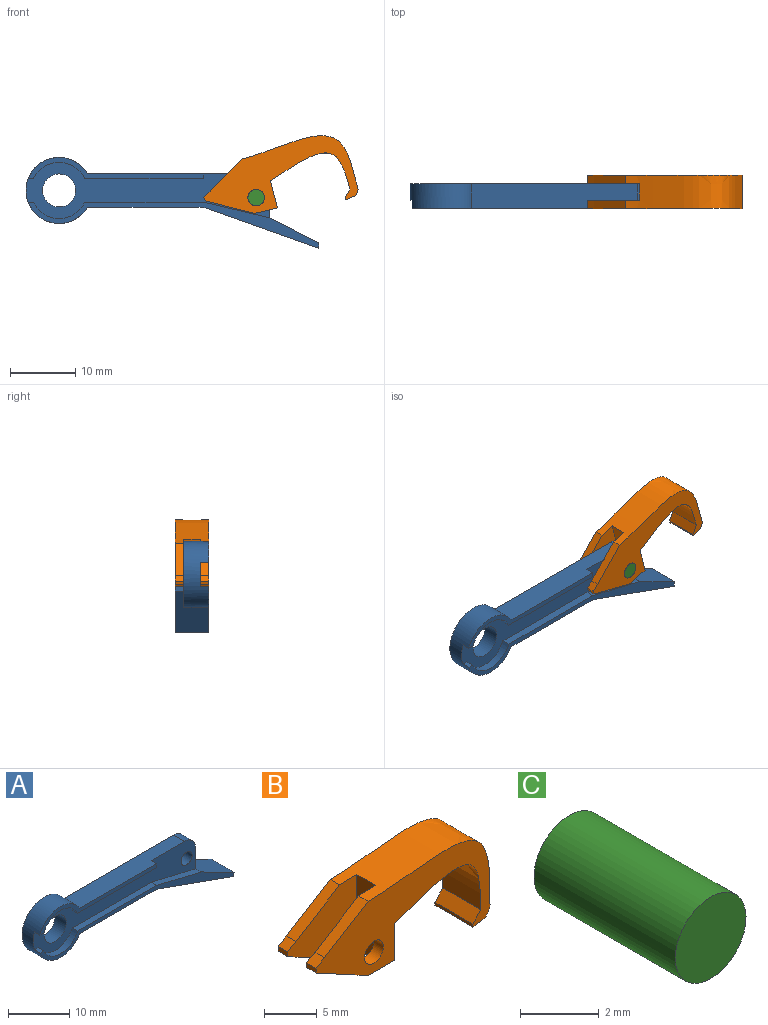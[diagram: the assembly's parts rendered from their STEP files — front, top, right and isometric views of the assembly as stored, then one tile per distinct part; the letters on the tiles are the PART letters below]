
ASSEMBLY  parts=3 mates=2
PART A: 26 faces, bbox 45x5.1x14 mm
  f0: plane 4.21x2.54mm, normal (1,0,0), area 10.7mm2, adj f1,f6,f7,f22
  f1: cylinder r=2.54mm len=2.54mm, axis (0,1,0), area 10.1mm2, adj f0,f2,f6,f7
  f2: plane 25.45x3.81mm, normal (0,0,1), area 87.2mm2, adj f1,f5,f6,f7,f11,f12
  f3: cylinder r=2.54mm len=5.08mm, axis (0,1,0), area 40.5mm2, adj f6,f7
  f4: cylinder r=1.27mm len=2.54mm, axis (0,1,0), area 20.3mm2, adj f6,f7
  f5: cylinder r=5.08mm len=10.16mm, axis (0,1,0), area 96.7mm2, adj f2,f6,f7,f8,f12,f13,f15,f17
  f6: plane 37.48x8.64mm, normal (0,-1,0), area 155.1mm2, adj f0,f1,f2,f3,f4,f5,f8,f9
  f7: plane 37.48x10.16mm, normal (0,1,0), area 198.9mm2, adj f0,f1,f2,f3,f4,f5,f15,f18
  f8: plane 1.27x0.82mm, normal (0,0,-1), area 1mm2, adj f5,f6,f9,f12
  f9: cylinder r=4.32mm len=7.88mm, axis (0,1,0), area 12.6mm2, adj f6,f8,f10,f12
  f10: plane 18.25x1.27mm, normal (0,0,-1), area 23.2mm2, adj f6,f9,f11,f12
  f11: plane 1.27x0.76mm, normal (1,0,0), area 1mm2, adj f2,f6,f10,f12
  f12: plane 26.94x3.31mm, normal (0,-1,0), area 21.9mm2, adj f2,f5,f8,f9,f10,f11
  f13: plane 1.27x0.82mm, normal (0,0,1), area 1mm2, adj f5,f6,f14,f17
  f14: cylinder r=4.32mm len=7.86mm, axis (0,1,0), area 12.6mm2, adj f6,f13,f16,f17
  f15: plane 16.9x3.81mm, normal (0,0,-1), area 64.4mm2, adj f5,f7,f17,f25
  f16: plane 18.26x1.27mm, normal (0,0,1), area 23.2mm2, adj f6,f14,f17,f23
  f17: plane 44.72x7.1mm, normal (0,-1,0), area 46.7mm2, adj f5,f13,f14,f15,f16,f20,f21,f22
  f18: plane 1.27x0.76mm, normal (-1,0,0.02), area 1mm2, adj f7,f19,f20,f24
  f19: plane 10.2x2.43mm, normal (0.23,0,0.97), area 13.3mm2, adj f7,f18,f22,f24
  f20: plane 17.78x6.34mm, normal (-0.34,0,-0.94), area 92.5mm2, adj f7,f17,f18,f21,f24,f25
  f21: plane 5.08x0.87mm, normal (1,0,-0.01), area 4.4mm2, adj f17,f20,f22,f24
  f22: plane 7.57x5.08mm, normal (0.45,0,0.89), area 43mm2, adj f0,f17,f19,f21,f23,f24
  f23: plane 10.2x2.43mm, normal (0.23,0,0.97), area 13.3mm2, adj f6,f16,f17,f22
  f24: plane 17.79x7.1mm, normal (0,1,0), area 24.8mm2, adj f18,f19,f20,f21,f22
  f25: cylinder r=5.08mm len=3.81mm, axis (0,1,0), area 6.6mm2, adj f7,f15,f17,f20
PART B: 23 faces, bbox 24x5.2x11.4 mm
  f0: plane 5.08x4.3mm, normal (1,0,0), area 21.9mm2, adj f1,f13,f14,f18
  f1: plane 5.08x3.55mm, normal (0,0,-1), area 12.2mm2, adj f0,f2,f11,f13,f14,f15,f16,f17
  f2: plane 6.95x3.76mm, normal (-0.48,0,-0.88), area 10mm2, adj f1,f3,f14,f17
  f3: plane 1.27x0.57mm, normal (-1,0,-0.08), area 0.7mm2, adj f2,f4,f14,f17
  f4: plane 1.27x1.13mm, normal (-0.5,0,0.86), area 1.7mm2, adj f3,f5,f14,f17
  f5: plane 5.86x3.62mm, normal (-0.53,0,0.85), area 8.8mm2, adj f4,f6,f14,f17
  f6: extruded ~16.32x9.3mm, area 113.5mm2, adj f5,f8,f13,f14,f15,f16,f17,f22
  f7: cylinder r=1.27mm len=2.54mm, axis (0,1,0), area 10.1mm2, adj f14,f17
  f8: plane 5.86x3.62mm, normal (-0.53,0,0.85), area 8.8mm2, adj f6,f9,f13,f16
  f9: plane 1.27x1.13mm, normal (-0.5,0,0.86), area 1.7mm2, adj f8,f10,f13,f16
  f10: plane 1.27x0.57mm, normal (-1,0,-0.08), area 0.7mm2, adj f9,f11,f13,f16
  f11: plane 6.95x3.76mm, normal (-0.48,0,-0.88), area 10mm2, adj f1,f10,f13,f16
  f12: cylinder r=1.27mm len=2.54mm, axis (0,1,0), area 10.1mm2, adj f13,f16
  f13: plane 23.89x11.33mm, normal (0,-1,0), area 107mm2, adj f0,f1,f6,f8,f9,f10,f11,f12
  f14: plane 23.89x11.33mm, normal (0,1,0), area 107mm2, adj f0,f1,f2,f3,f4,f5,f6,f7
  f15: plane 8.68x2.54mm, normal (-1,0,0), area 22mm2, adj f1,f6,f16,f17
  f16: plane 9.39x8.79mm, normal (0,1,0), area 46.5mm2, adj f1,f6,f8,f9,f10,f11,f12,f15
  f17: plane 9.38x8.79mm, normal (0,-1,0), area 46.5mm2, adj f1,f2,f3,f4,f5,f6,f7,f15
  f18: extruded ~11.52x6.39mm, area 85.3mm2, adj f0,f13,f14,f19
  f19: plane 5.08x1.16mm, normal (-0.74,0,0.67), area 7.9mm2, adj f13,f14,f18,f20
  f20: plane 5.08x0.33mm, normal (-1,0,0), area 1.7mm2, adj f13,f14,f19,f21
  f21: plane 5.08x1.2mm, normal (0.14,0,-0.99), area 6.2mm2, adj f13,f14,f20,f22
  f22: cylinder r=1.27mm len=5.08mm, axis (0,1,0), area 9.4mm2, adj f6,f13,f14,f21
PART C: 3 faces, bbox 2.5x5.1x2.5 mm
  f0: cylinder r=1.27mm len=5.08mm, axis (0,1,0), area 40.5mm2, adj f1,f2
  f1: plane 2.54x2.54mm, normal (0,-1,0), area 5.1mm2, adj f0
  f2: plane 2.54x2.54mm, normal (0,1,0), area 5.1mm2, adj f0
PLACE A at identity fixed
PLACE B rot(axis=(0,-1,0),14.2deg) t=(8.91,0,-1.21)mm
PLACE C t=(7.4,2.54,0)mm
MATE fastened A.f4 <-> C.f0  axis (0,-1,0) through (7.4,-1.27,0)mm
MATE revolute C.f0 <-> B.f7  axis (0,1,0) through (7.4,2.54,0)mm
